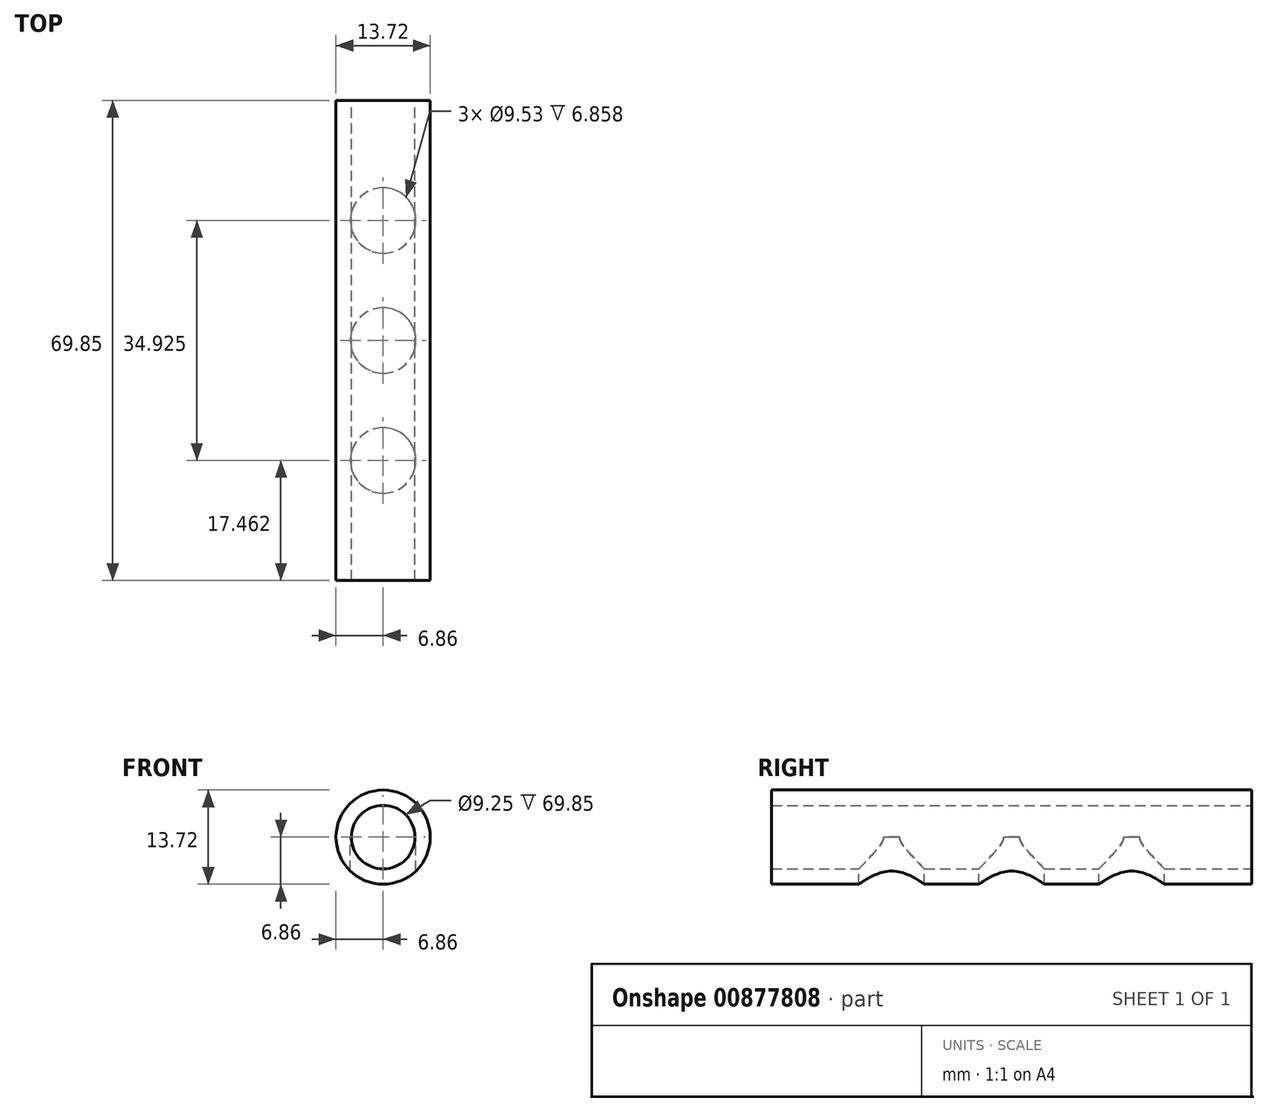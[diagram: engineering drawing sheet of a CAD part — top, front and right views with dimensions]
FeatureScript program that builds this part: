
annotation { "Feature Type Name" : "Feature", "Feature Type Description" : "" }
export const myFeature = defineFeature(function(context is Context, id is Id, definition is map)
    precondition{}
    {
        {
            var Q0;
            Q0=qCreatedBy(makeId("Front.planeOp"),FACE);
            var sketch = newSketch(context, id + "F0", { "sketchPlane" : qUnion([Q0])});
            skCircle(sketch, "E0", {"center": v(0, 0) * mm, "radius": 6.86 * mm});
            skCircle(sketch, "E1", {"center": v(0, 0) * mm, "radius": 4.62 * mm});
            skSolve(sketch);
        }
        {
            var Q0;
            Q0=makeQuery(id+"F0.imprint","IMPRINT",FACE,{"disambiguationData":[TD([[makeQuery(id+"F0.imprint","IMPRINT",EDGE,{"derivedFrom":sQuery(id+"F0.wireOp",EDGE,"E0")}),1.0]])]});
            extrude(context, id + "F1", {"entities" : qUnion([Q0]), "depth" : 69.85 * mm, "offsetDistance" : 25.4 * mm});
        }
        {
            var Q0;
            Q0=qCreatedBy(makeId("Top.planeOp"),FACE);
            var sketch = newSketch(context, id + "F2", { "sketchPlane" : qUnion([Q0])});
            skCircle(sketch, "E2", {"center": v(0, -17.46) * mm, "radius": 4.76 * mm});
            skCircle(sketch, "E3", {"center": v(0, -34.93) * mm, "radius": 4.76 * mm});
            skCircle(sketch, "E4", {"center": v(0, -52.39) * mm, "radius": 4.76 * mm});
            skSolve(sketch);
        }
        {
            var Q0;
            Q0 = qSketchRegion(id + "F2", true);
            extrude(context, id + "F3", {"entities" : qUnion([Q0]), "operationType" : NewBodyOperationType.REMOVE, "oppositeDirection" : true, "depth" : 25.4 * mm, "offsetDistance" : 25.4 * mm});
        }
    });
